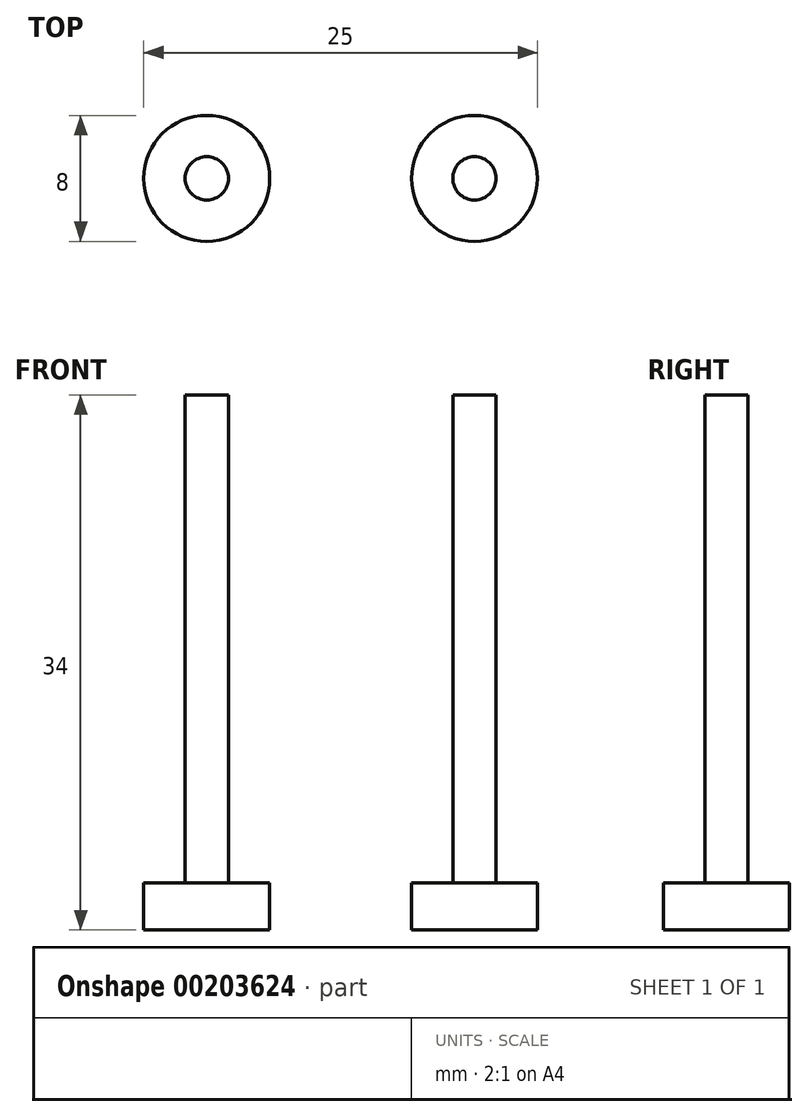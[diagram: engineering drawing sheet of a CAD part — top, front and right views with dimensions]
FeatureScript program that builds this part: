
annotation { "Feature Type Name" : "Feature", "Feature Type Description" : "" }
export const myFeature = defineFeature(function(context is Context, id is Id, definition is map)
    precondition{}
    {
        {
            var Q0;
            Q0=qCreatedBy(makeId("Top.planeOp"),FACE);
            var sketch = newSketch(context, id + "F0", { "sketchPlane" : qUnion([Q0])});
            skCircle(sketch, "E0", {"center": v(0, 0) * mm, "radius": 4 * mm});
            skCircle(sketch, "E1", {"center": v(0, 0) * mm, "radius": 1.38 * mm});
            skSolve(sketch);
        }
        {
            var Q0;
            Q0=makeQuery(id+"F0.imprint","IMPRINT",FACE,{"disambiguationData":[TD([[makeQuery(id+"F0.imprint","IMPRINT",EDGE,{"derivedFrom":sQuery(id+"F0.wireOp",EDGE,"E0")}),1.0]])]});
            var Q1;
            Q1=makeQuery(id+"F0.imprint","IMPRINT",FACE,{"disambiguationData":[TD([[makeQuery(id+"F0.imprint","IMPRINT",EDGE,{"derivedFrom":sQuery(id+"F0.wireOp",EDGE,"E1")}),1.0]])]});
            extrude(context, id + "F1", {"entities" : qUnion([Q0, Q1]), "depth" : 3 * mm});
        }
        {
            var Q0;
            Q0=makeQuery(id+"F0.imprint","IMPRINT",FACE,{"disambiguationData":[TD([[makeQuery(id+"F0.imprint","IMPRINT",EDGE,{"derivedFrom":sQuery(id+"F0.wireOp",EDGE,"E1")}),1.0]])]});
            extrude(context, id + "F2", {"entities" : qUnion([Q0]), "operationType" : NewBodyOperationType.ADD, "depth" : 34 * mm});
        }
        {
            var Q0;
            Q0=makeQuery(id+"F1.opExtrude","SWEPT_BODY",BODY,{"disambiguationData":[OSD([sQuery(id+"F0.wireOp",EDGE,"E0")])]});
            transform(context, id + "F3", {"entities" : qUnion([Q0]), "transformType" : TransformType.TRANSLATION_3D, "dx" : 17 * mm, "dy" : 0 * mm, "dz" : 0 * mm, "makeCopy" : true});
        }
    });
